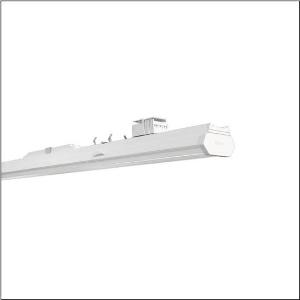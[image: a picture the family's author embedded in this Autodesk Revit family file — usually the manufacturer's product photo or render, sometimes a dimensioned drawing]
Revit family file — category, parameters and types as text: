
# Revit family: licross_r__11_protected_extreme_ho_51tp12dn4fxme_36ff
name_source: partatom
category: Lighting Fixtures
units: mm (PartAtom-declared; Revit-internal decimal feet)

## family parameters
Cut with Voids When Loaded = No
Host = Face
Light Source = No
Part Type = Normal
Room Calculation Point = No
Round Connector Dimension = Use Diameter
Shared = No

## types (1)
- --- (1 x LED, 15270 lm, 87.3 W, 4000K)
    Apparent Load = 87 VA
    CIE Flux Codes = 70 91 97 98 100
    Color Rendering = 80
    Color Temperature = 4000K
    Default Elevation = 1800 mm
    Description = Licross® 11 Protected extreme HO, luminaire insert, of sheet steel, galvanised, coil coated, white, length: 1.500mm, width: 90mm, height: 101mm, LED rated luminous flux: 15.270lm, light colour: 840, control gear: DALI 2, with plug, 5-pole, with phase selection, mains connection: 220..240V, AC, 50/60Hz, rated input power: 87W, halogen-free wiring, primary optical cover: cover, of PMMA, light emission: direct distribution, primary light characteristic: symmetric, protection rating (complete): IP64, insulation class (complete): insulation class I (protective earthing), certification: CE, ENEC, VDE, UKCA, protection symbol: D if used in an environment with conductive dust loads with corresponding accessories, impact resistance: IK06, permissible ambient temperature for indoor applications: -40..+40°C, corresponds to IFS (International Featured Standards) requirements for safety and quality in the food industry, reducing of maximum allowable ambient temperature of 5°C with ceiling mounting, LABS conformity tested according to VDMA 24364:2018-05, packaging unit: 1 piece
    Height = 92 mm
    Lamp = 1 x LED
    Lamp Light Flux = 15270 lm
    Lamp Power = 87.3 W
    Lamp count = 1
    Length = 1500 mm
    Luminous efficacy = 175 lm/W
    Manufacturer = Siteco
    ModVariant = No
    Model = 51TP12DN4FXME
    Mounting Place = Ceiling
    Mounting Type = Pendant
    Number of Poles = 1
    OnlyDefault = Yes
    Power Factor = 1
    Product Name = Licross® 11 Protected extreme HO
    Product group = luminaire insert
    ProductGroupID = 901
    Protection Class = Protection class I
    Protection Degree = IP 64
    RLX_Detail_Level = 1
    RLX_Emergency_Light_Flux = 0 lm
    RLX_Emergency_Type = 0
    RLX_Emergency_Type_DB = No
    RlxData = <blob elided: 24425 chars, md5=cd1f5a58>
    Socket = socket
    Standby Power = 0 W
    System Light Flux = 15270 lm
    System Power = 87 W
    Type Comments = factory setting: luminous flux: 100 % | dim-lin: 254 | 589 mA
    Type Image = l_1256148.jpg
    URL = http://relux.com
    VarID = @adj_035051
    Voltage = 0 V
    Weight = 0.00 kg
    Width = 88 mm

## geometry (parser evidence)
native form markers: Blend x4, Sweep x10
no freeform markers — native parametric forms only
